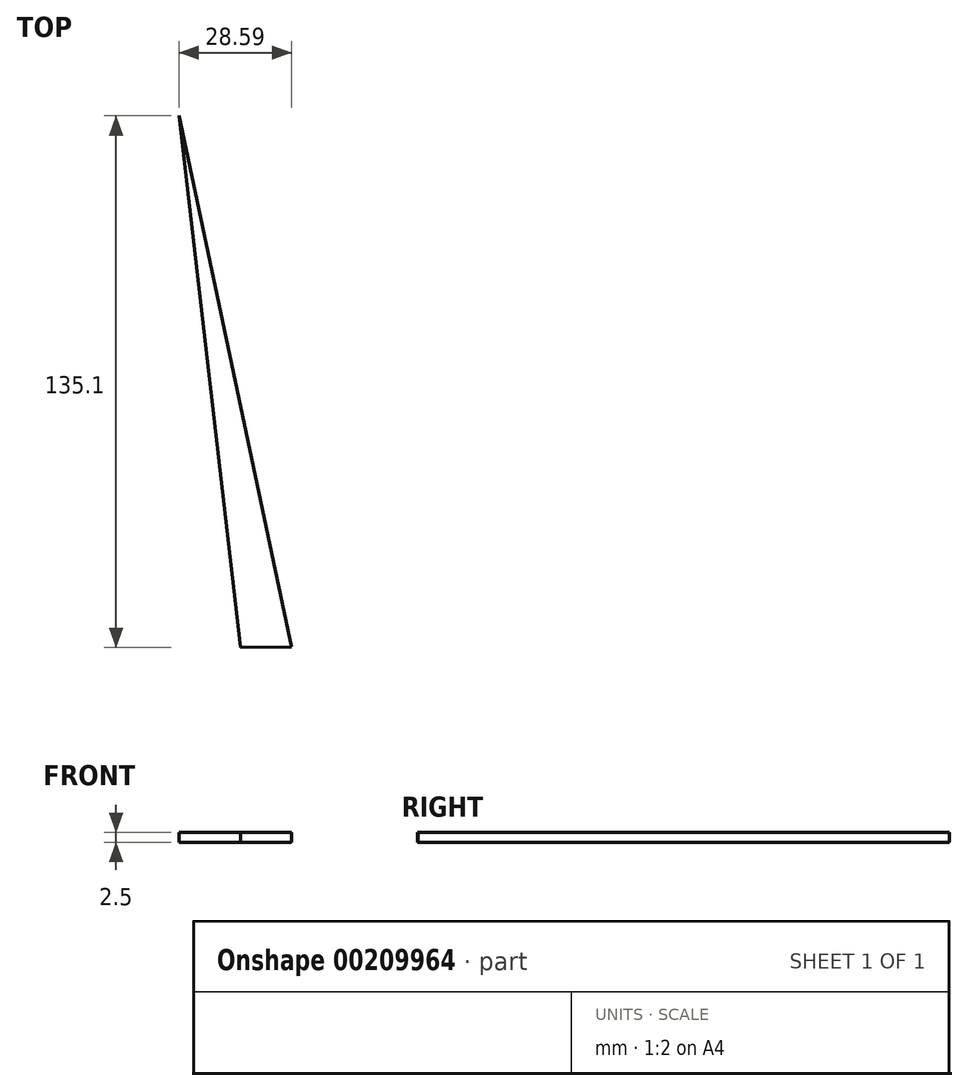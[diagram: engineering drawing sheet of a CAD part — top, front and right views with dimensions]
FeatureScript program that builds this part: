
annotation { "Feature Type Name" : "Feature", "Feature Type Description" : "" }
export const myFeature = defineFeature(function(context is Context, id is Id, definition is map)
    precondition{}
    {
        {
            var Q0;
            Q0=qCreatedBy(makeId("Top.planeOp"),FACE);
            var sketch = newSketch(context, id + "F0", { "sketchPlane" : qUnion([Q0])});
            skLineSegment(sketch, "E0", {"start": v(-45.72, -45.69) * mm, "end": v(-74.3, 89.32) * mm});
            skLineSegment(sketch, "E1", {"start": v(-74.3, 89.32) * mm, "end": v(-58.72, -45.78) * mm});
            skLineSegment(sketch, "E2", {"start": v(-45.72, -45.69) * mm, "end": v(-58.72, -45.78) * mm});
            skSolve(sketch);
        }
        {
            var Q0;
            Q0=makeQuery(id+"F0.imprint","IMPRINT",FACE,{"disambiguationData":[TD([[makeQuery(id+"F0.imprint","IMPRINT",EDGE,{"derivedFrom":sQuery(id+"F0.wireOp",EDGE,"E0")}),1.0]])]});
            extrude(context, id + "F1", {"entities" : qUnion([Q0]), "depth" : 2.5 * mm});
        }
    });
